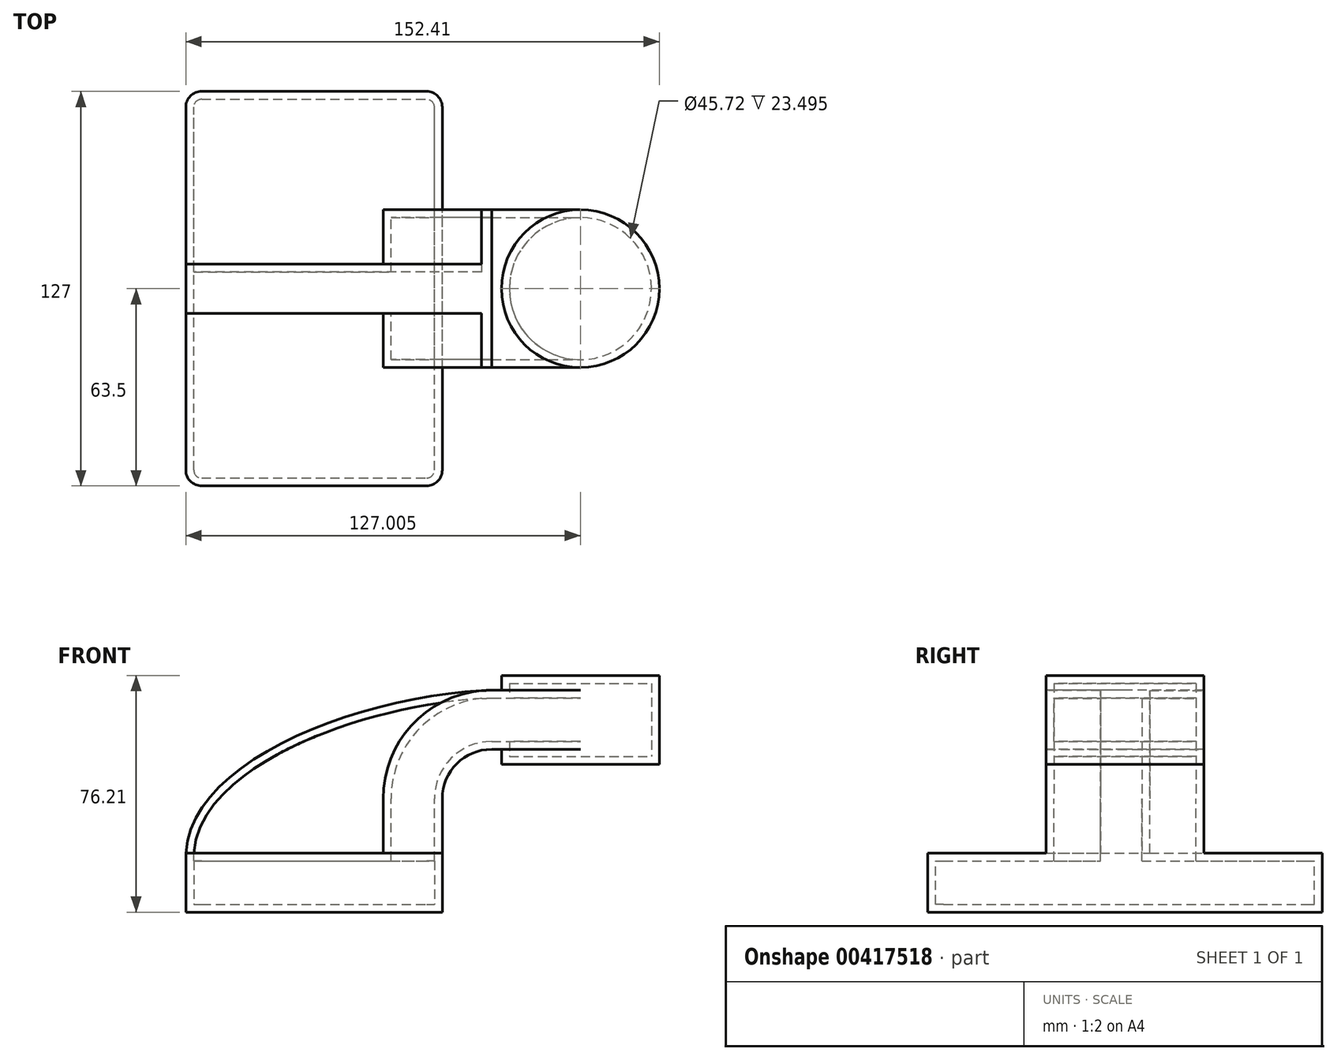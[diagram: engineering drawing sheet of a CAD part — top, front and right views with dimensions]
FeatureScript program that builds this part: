
annotation { "Feature Type Name" : "Feature", "Feature Type Description" : "" }
export const myFeature = defineFeature(function(context is Context, id is Id, definition is map)
    precondition{}
    {
        {
            var Q0;
            Q0=qCreatedBy(makeId("Front.planeOp"),FACE);
            var sketch = newSketch(context, id + "F0", { "sketchPlane" : qUnion([Q0])});
            skLineSegment(sketch, "E0.rect.bottom", {"start": v(-41.28, 9.52) * mm, "end": v(41.28, 9.52) * mm});
            skLineSegment(sketch, "E0.rect.top", {"start": v(-41.28, -9.52) * mm, "end": v(41.28, -9.52) * mm});
            skLineSegment(sketch, "E0.rect.left", {"start": v(-41.28, 9.52) * mm, "end": v(-41.28, -9.52) * mm});
            skLineSegment(sketch, "E0.rect.right", {"start": v(41.28, 9.52) * mm, "end": v(41.28, -9.52) * mm});
            skPoint(sketch, "E0.rect.middle", {"position": v(0, 0) * mm});
            skLineSegment(sketch, "E1", {"start": v(41.28, 9.52) * mm, "end": v(41.28, 27) * mm});
            skArc(sketch, "E2", {"start": v(41.28, 27) * mm, "mid": v(45.92, 38.23) * mm, "end": v(57.15, 42.88) * mm});
            skLineSegment(sketch, "E3", {"start": v(57.15, 42.88) * mm, "end": v(85.72, 42.88) * mm});
            skLineSegment(sketch, "E4.rect.bottom", {"start": v(60.32, 38.1) * mm, "end": v(111.12, 38.1) * mm});
            skLineSegment(sketch, "E4.rect.top", {"start": v(60.32, 66.68) * mm, "end": v(111.12, 66.68) * mm});
            skLineSegment(sketch, "E4.rect.left", {"start": v(60.32, 38.1) * mm, "end": v(60.32, 66.68) * mm});
            skLineSegment(sketch, "E4.rect.right", {"start": v(111.13, 38.1) * mm, "end": v(111.12, 66.68) * mm});
            skPoint(sketch, "E4.rect.middle", {"position": v(85.72, 52.39) * mm});
            skLineSegment(sketch, "E5.0", {"start": v(57.15, 61.93) * mm, "end": v(85.72, 61.93) * mm});
            skArc(sketch, "E5.1", {"start": v(22.23, 27) * mm, "mid": v(32.45, 51.7) * mm, "end": v(57.15, 61.93) * mm});
            skLineSegment(sketch, "E5.2", {"start": v(22.23, 9.52) * mm, "end": v(22.23, 27) * mm});
            skLineSegment(sketch, "E6", {"start": v(85.72, 38.1) * mm, "end": v(85.72, 66.68) * mm});
            skFitSpline(sketch, "E7", {"points": [v(-41.28, 9.53) * mm, v(57.15, 61.93) * mm], "startDerivative": vector(5.2, 92.34) * mm, "endDerivative": vector(120.92, 4.22) * mm});
            skSolve(sketch);
        }
        {
            var Q0;
            Q0=makeQuery(id+"F0.imprint","IMPRINT",FACE,{"disambiguationData":[TD([[makeQuery(id+"F0.imprint","IMPRINT",EDGE,{"derivedFrom":sQuery(id+"F0.wireOp",EDGE,"E0.rect.top")}),1.0]])]});
            extrude(context, id + "F1", {"entities" : qUnion([Q0]), "endBound" : BoundingType.SYMMETRIC, "depth" : 127 * mm});
        }
        {
            var Q0;
            {var subQ9=sQuery(id+"F0.wireOp",EDGE,"E1");Q0=makeQuery(id+"F0.imprint","IMPRINT",FACE,{"disambiguationData":[TD([[makeQuery(id+"F0.imprint","IMPRINT",EDGE,{"derivedFrom":subQ9}),1.0]])]});}
            var Q1;
            {var subQ0=sQuery(id+"F0.wireOp",EDGE,"E6");var subQ1=sQuery(id+"F0.wireOp",EDGE,"E3");var subQ2=makeQuery(id+"F0.imprint","INTERSECT",VERTEX,{"derivedFrom":[subQ1,subQ0]});Q1=makeQuery(id+"F0.imprint","IMPRINT",FACE,{"disambiguationData":[TD([[makeQuery(id+"F0.imprint","IMPRINT",EDGE,{"disambiguationData":[TD([[subQ2,1.0]])],"derivedFrom":subQ1}),1.0]])]});}
            extrude(context, id + "F2", {"entities" : qUnion([Q0, Q1]), "operationType" : NewBodyOperationType.ADD, "endBound" : BoundingType.SYMMETRIC, "depth" : 50.8 * mm});
        }
        {
            var Q0;
            {var subQ3=sQuery(id+"F0.wireOp",EDGE,"E5.2");Q0=makeQuery(id+"F0.imprint","IMPRINT",FACE,{"disambiguationData":[TD([[makeQuery(id+"F0.imprint","IMPRINT",EDGE,{"derivedFrom":subQ3}),1.0]])]});}
            extrude(context, id + "F3", {"entities" : qUnion([Q0]), "operationType" : NewBodyOperationType.ADD, "endBound" : BoundingType.SYMMETRIC, "depth" : 15.88 * mm});
        }
        {
            var Q0;
            {var subQ5=sQuery(id+"F0.wireOp",EDGE,"E4.rect.right");Q0=makeQuery(id+"F0.imprint","IMPRINT",FACE,{"disambiguationData":[TD([[makeQuery(id+"F0.imprint","IMPRINT",EDGE,{"derivedFrom":subQ5}),1.0]])]});}
            var Q1;
            Q1=sQuery(id+"F0.wireOp",EDGE,"E6");
            revolve(context, id + "F4", {"operationType" : NewBodyOperationType.ADD, "entities" : qUnion([Q0]), "axis" : qUnion([Q1]), "revolveType" : RevolveType.FULL});
        }
        {
            var Q0;
            Q0=makeQuery(id+"F1.opExtrude","CAP_EDGE",EDGE,{"disambiguationData":[OSD([sQuery(id+"F0.wireOp",EDGE,"E0.rect.right")])],"isStart":false});
            var Q1;
            Q1=makeQuery(id+"F1.opExtrude","CAP_EDGE",EDGE,{"disambiguationData":[OSD([sQuery(id+"F0.wireOp",EDGE,"E0.rect.left")])],"isStart":false});
            var Q2;
            Q2=makeQuery(id+"F1.opExtrude","CAP_EDGE",EDGE,{"disambiguationData":[OSD([sQuery(id+"F0.wireOp",EDGE,"E0.rect.right")])],"isStart":true});
            var Q3;
            Q3=makeQuery(id+"F1.opExtrude","CAP_EDGE",EDGE,{"disambiguationData":[OSD([sQuery(id+"F0.wireOp",EDGE,"E0.rect.left")])],"isStart":true});
            fillet(context, id + "F5", {"entities" : qUnion([Q0, Q1, Q2, Q3]), "radius" : 5.08 * mm, "tangentPropagation" : true, "allowEdgeOverflow" : false});
        }
        {
            var Q0;
            Q0=makeQuery(id+"F3.opExtrude","CAP_FACE",FACE,{"disambiguationData":[OSD([sQuery(id+"F0.wireOp",EDGE,"E0.rect.bottom"),sQuery(id+"F0.wireOp",EDGE,"E5.1"),sQuery(id+"F0.wireOp",EDGE,"E5.2"),sQuery(id+"F0.wireOp",EDGE,"E7")])],"isStart":false});
            shell(context, id + "F6", {"entities" : qUnion([Q0]), "thickness" : 2.54 * mm});
        }
    });
